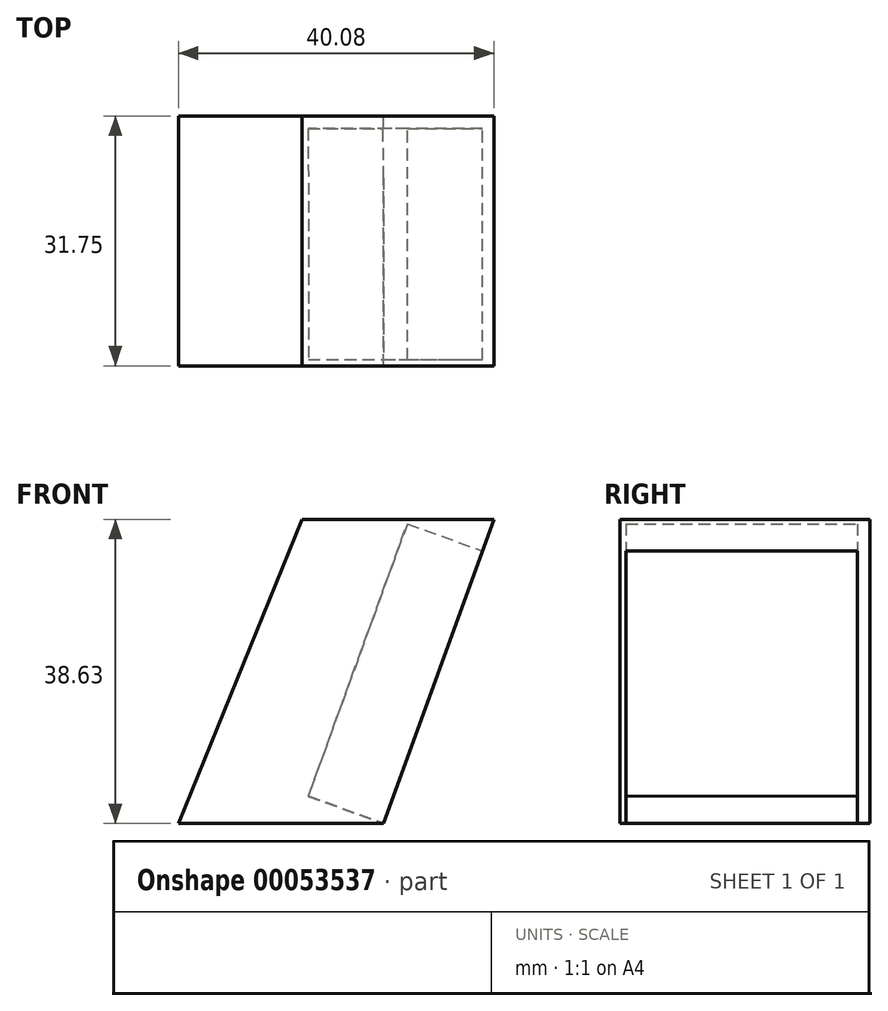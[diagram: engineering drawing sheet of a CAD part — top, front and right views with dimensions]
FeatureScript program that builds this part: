
annotation { "Feature Type Name" : "Feature", "Feature Type Description" : "" }
export const myFeature = defineFeature(function(context is Context, id is Id, definition is map)
    precondition{}
    {
        {
            var Q0;
            Q0=qCreatedBy(makeId("Front.planeOp"),FACE);
            var sketch = newSketch(context, id + "F0", { "sketchPlane" : qUnion([Q0])});
            skLineSegment(sketch, "E0", {"start": v(0, 0) * mm, "end": v(20.32, 0) * mm});
            skLineSegment(sketch, "E1", {"start": v(9.97, 38.63) * mm, "end": v(30.3, 38.63) * mm});
            skLineSegment(sketch, "E2", {"start": v(30.3, 38.63) * mm, "end": v(34.35, 38.6) * mm});
            skPoint(sketch, "E3.1.internal.orphan", {"position": v(0, 13.01) * mm});
            skPoint(sketch, "E4.1.internal.orphan", {"position": v(20.32, 2.98) * mm});
            skLineSegment(sketch, "E5", {"start": v(-5.73, 0) * mm, "end": v(0, 0) * mm});
            skLineSegment(sketch, "E6", {"start": v(34.35, 38.6) * mm, "end": v(20.32, 0) * mm});
            skLineSegment(sketch, "E7", {"start": v(9.97, 38.63) * mm, "end": v(-5.73, 0) * mm});
            skSolve(sketch);
        }
        {
            var Q0;
            Q0 = qSketchRegion(id + "F0", true);
            extrude(context, id + "F1", {"entities" : qUnion([Q0]), "depth" : 31.75 * mm});
        }
        {
            var Q0;
            Q0=makeQuery(id+"F1.opExtrude","SWEPT_FACE",FACE,{"disambiguationData":[OSD([sQuery(id+"F0.wireOp",EDGE,"E6")])]});
            cPlane(context, id + "F2", {"entities" : qUnion([Q0]), "cplaneType" : CPlaneType.OFFSET, "offset" : 0 * mm, "width" : 152.4 * mm, "height" : 152.4 * mm});
        }
        {
            var Q0;
            Q0=qCreatedBy(id+"F2.planeOp",FACE);
            var sketch = newSketch(context, id + "F3", { "sketchPlane" : qUnion([Q0])});
            skLineSegment(sketch, "E8", {"start": v(-30.96, 6.99) * mm, "end": v(-30.96, 43.76) * mm});
            skLineSegment(sketch, "E9", {"start": v(-1.6, 43.76) * mm, "end": v(-1.6, 6.93) * mm});
            skLineSegment(sketch, "E10", {"start": v(-1.6, 6.93) * mm, "end": v(-30.96, 6.99) * mm});
            skLineSegment(sketch, "E11", {"start": v(-30.96, 43.76) * mm, "end": v(-1.6, 43.76) * mm});
            skSolve(sketch);
        }
        {
            var Q0;
            Q0 = qSketchRegion(id + "F3", true);
            extrude(context, id + "F4", {"entities" : qUnion([Q0]), "operationType" : NewBodyOperationType.REMOVE, "oppositeDirection" : true, "depth" : 10.16 * mm});
        }
    });
